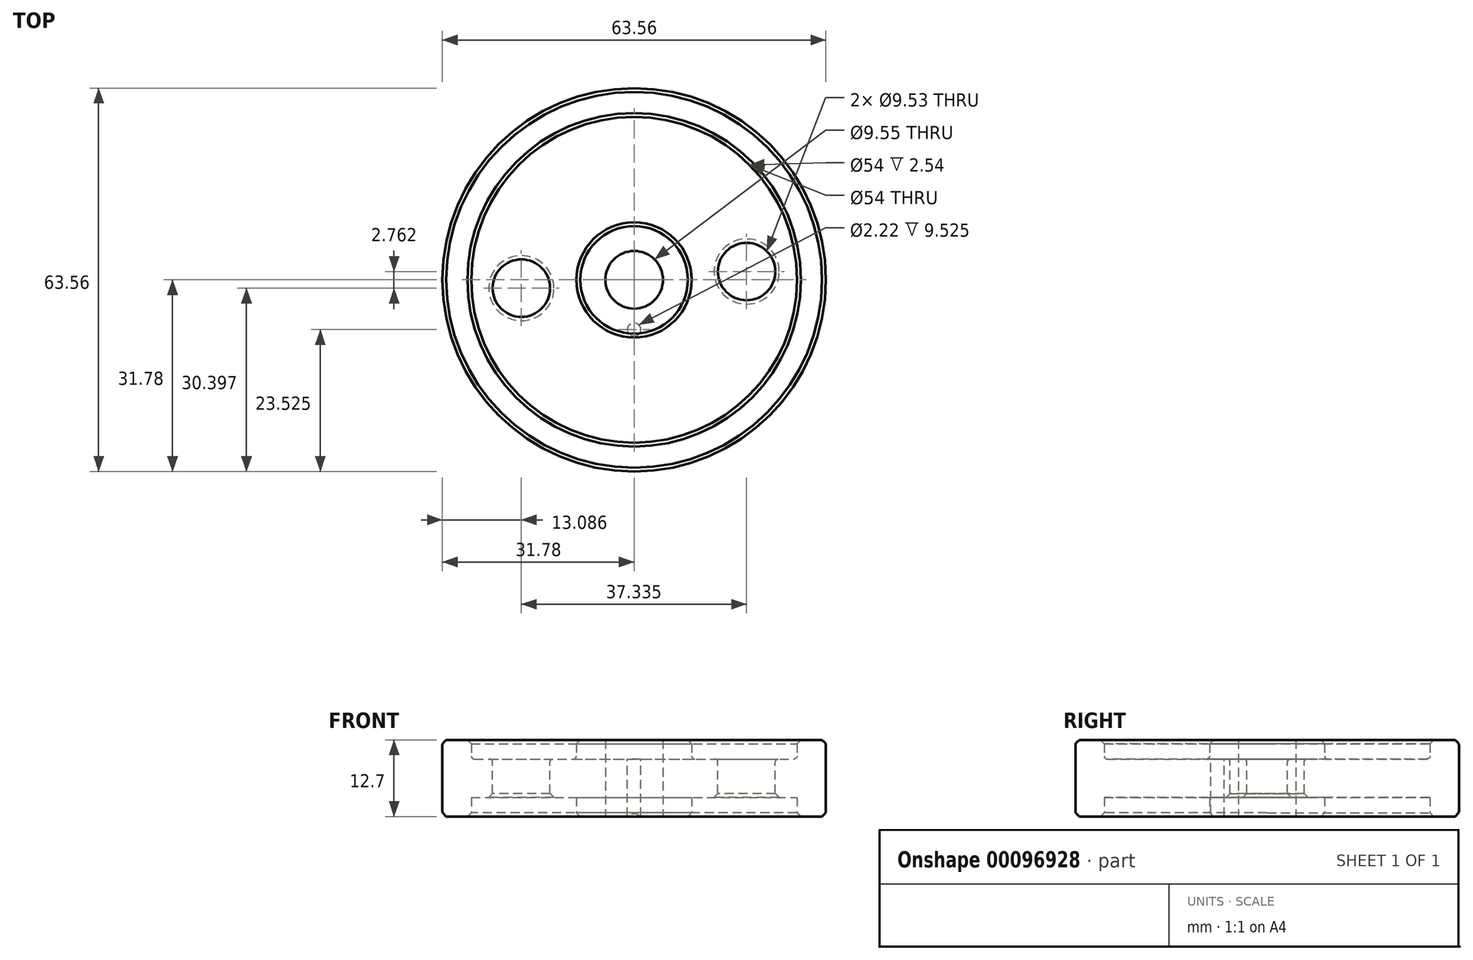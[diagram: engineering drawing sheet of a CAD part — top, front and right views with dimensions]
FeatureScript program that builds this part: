
annotation { "Feature Type Name" : "Feature", "Feature Type Description" : "" }
export const myFeature = defineFeature(function(context is Context, id is Id, definition is map)
    precondition{}
    {
        {
            var Q0;
            Q0=qCreatedBy(makeId("Front.planeOp"),FACE);
            var sketch = newSketch(context, id + "F0", { "sketchPlane" : qUnion([Q0])});
            skLineSegment(sketch, "E0", {"start": v(0, 0) * mm, "end": v(0, 8.6) * mm, "construction": true});
            skLineSegment(sketch, "E1", {"start": v(0, 0) * mm, "end": v(4.78, 0) * mm, "construction": true});
            skLineSegment(sketch, "E2", {"start": v(4.78, 0) * mm, "end": v(4.78, 12.7) * mm});
            skLineSegment(sketch, "E3", {"start": v(4.78, 12.7) * mm, "end": v(9.55, 12.7) * mm});
            skLineSegment(sketch, "E4", {"start": v(9.55, 12.7) * mm, "end": v(9.55, 9.53) * mm});
            skLineSegment(sketch, "E5", {"start": v(9.55, 9.53) * mm, "end": v(27, 9.53) * mm});
            skLineSegment(sketch, "E6", {"start": v(27, 9.53) * mm, "end": v(27, 12.7) * mm});
            skLineSegment(sketch, "E7", {"start": v(27, 12.7) * mm, "end": v(31.78, 12.7) * mm});
            skLineSegment(sketch, "E8", {"start": v(31.78, 12.7) * mm, "end": v(31.78, 0) * mm});
            skLineSegment(sketch, "E9", {"start": v(31.78, 0) * mm, "end": v(27, 0) * mm});
            skLineSegment(sketch, "E10", {"start": v(27, 0) * mm, "end": v(27, 3.18) * mm});
            skLineSegment(sketch, "E11", {"start": v(27, 3.18) * mm, "end": v(9.55, 3.18) * mm});
            skLineSegment(sketch, "E12", {"start": v(9.55, 3.18) * mm, "end": v(9.55, 0) * mm});
            skLineSegment(sketch, "E13", {"start": v(9.55, 0) * mm, "end": v(4.78, 0) * mm});
            skSolve(sketch);
        }
        {
            var Q0;
            Q0=makeQuery(id+"F0.imprint","IMPRINT",FACE,{"disambiguationData":[TD([[makeQuery(id+"F0.imprint","IMPRINT",EDGE,{"derivedFrom":sQuery(id+"F0.wireOp",EDGE,"E2")}),-1.0]])]});
            var Q1;
            Q1=sQuery(id+"F0.wireOp",EDGE,"E0");
            revolve(context, id + "F1", {"entities" : qUnion([Q0]), "axis" : qUnion([Q1]), "revolveType" : RevolveType.FULL});
        }
        {
            var Q0;
            Q0=makeQuery(id+"F1.opRevolve","SWEPT_FACE",FACE,{"disambiguationData":[OSD([sQuery(id+"F0.wireOp",EDGE,"E5")])]});
            var sketch = newSketch(context, id + "F2", { "sketchPlane" : qUnion([Q0])});
            skLineSegment(sketch, "E14", {"start": v(0, 0) * mm, "end": v(-47.23, -3.5) * mm, "construction": true});
            skLineSegment(sketch, "E15", {"start": v(0, 0) * mm, "end": v(41.04, 3.04) * mm, "construction": true});
            skCircle(sketch, "E16", {"center": v(-18.7, -1.38) * mm, "radius": 4.76 * mm});
            skCircle(sketch, "E17", {"center": v(18.64, 1.38) * mm, "radius": 4.76 * mm});
            skSolve(sketch);
        }
        {
            var Q0;
            Q0 = qSketchRegion(id + "F2", true);
            extrude(context, id + "F3", {"entities" : qUnion([Q0]), "operationType" : NewBodyOperationType.REMOVE, "endBound" : BoundingType.THROUGH_ALL, "oppositeDirection" : true, "depth" : 25.4 * mm});
        }
        {
            var Q0;
            Q0=makeQuery(id+"F3.boolean.opBoolean","COPY",EDGE,{"derivedFrom":makeQuery(id+"F3.opExtrude","CAP_EDGE",EDGE,{"disambiguationData":[OSD([sQuery(id+"F2.wireOp",EDGE,"E16")])],"isStart":true})});
            var Q1;
            Q1=makeQuery(id+"F3.boolean.opBoolean","COPY",EDGE,{"derivedFrom":makeQuery(id+"F3.opExtrude","CAP_EDGE",EDGE,{"disambiguationData":[OSD([sQuery(id+"F2.wireOp",EDGE,"E17")])],"isStart":true})});
            var Q2;
            Q2=makeQuery(id+"F1.opRevolve","SWEPT_EDGE",EDGE,{"disambiguationData":[OSD([sQuery(id+"F0.wireOp",EDGE,"E3"),sQuery(id+"F0.wireOp",EDGE,"E4")])]});
            chamfer(context, id + "F4", {"entities" : qUnion([Q0, Q1, Q2]), "width" : 0.64 * mm, "tangentPropagation" : true});
        }
        {
            var Q0;
            Q0=makeQuery(id+"F1.opRevolve","SWEPT_EDGE",EDGE,{"disambiguationData":[OSD([sQuery(id+"F0.wireOp",EDGE,"E6"),sQuery(id+"F0.wireOp",EDGE,"E7")])]});
            var Q1;
            Q1=makeQuery(id+"F1.opRevolve","SWEPT_EDGE",EDGE,{"disambiguationData":[OSD([sQuery(id+"F0.wireOp",EDGE,"E7"),sQuery(id+"F0.wireOp",EDGE,"E8")])]});
            chamfer(context, id + "F5", {"entities" : qUnion([Q0, Q1]), "width" : 0.64 * mm, "tangentPropagation" : true});
        }
        {
            var Q0;
            Q0=makeQuery(id+"F1.opRevolve","SWEPT_EDGE",EDGE,{"disambiguationData":[OSD([sQuery(id+"F0.wireOp",EDGE,"E8"),sQuery(id+"F0.wireOp",EDGE,"E9")])]});
            var Q1;
            Q1=makeQuery(id+"F1.opRevolve","SWEPT_EDGE",EDGE,{"disambiguationData":[OSD([sQuery(id+"F0.wireOp",EDGE,"E9"),sQuery(id+"F0.wireOp",EDGE,"E10")])]});
            var Q2;
            Q2=makeQuery(id+"F3.boolean.opBoolean","INTERSECT",EDGE,{"derivedFrom":[makeQuery(id+"F1.opRevolve","SWEPT_FACE",FACE,{"disambiguationData":[OSD([sQuery(id+"F0.wireOp",EDGE,"E11")])]}),makeQuery(id+"F3.opExtrude","SWEPT_FACE",FACE,{"disambiguationData":[OSD([sQuery(id+"F2.wireOp",EDGE,"E17")])]})]});
            var Q3;
            Q3=makeQuery(id+"F1.opRevolve","SWEPT_EDGE",EDGE,{"disambiguationData":[OSD([sQuery(id+"F0.wireOp",EDGE,"E12"),sQuery(id+"F0.wireOp",EDGE,"E13")])]});
            var Q4;
            Q4=makeQuery(id+"F3.boolean.opBoolean","INTERSECT",EDGE,{"derivedFrom":[makeQuery(id+"F1.opRevolve","SWEPT_FACE",FACE,{"disambiguationData":[OSD([sQuery(id+"F0.wireOp",EDGE,"E11")])]}),makeQuery(id+"F3.opExtrude","SWEPT_FACE",FACE,{"disambiguationData":[OSD([sQuery(id+"F2.wireOp",EDGE,"E16")])]})]});
            chamfer(context, id + "F6", {"entities" : qUnion([Q0, Q1, Q2, Q3, Q4]), "width" : 0.64 * mm, "tangentPropagation" : true});
        }
        {
            var Q0;
            Q0=makeQuery(id+"F1.opRevolve","SWEPT_FACE",FACE,{"disambiguationData":[OSD([sQuery(id+"F0.wireOp",EDGE,"E5")])]});
            var sketch = newSketch(context, id + "F7", { "sketchPlane" : qUnion([Q0])});
            skCircle(sketch, "E18", {"center": v(0, -8.26) * mm, "radius": 1.11 * mm});
            skSolve(sketch);
        }
        {
            var Q0;
            Q0 = qSketchRegion(id + "F7", true);
            extrude(context, id + "F8", {"entities" : qUnion([Q0]), "operationType" : NewBodyOperationType.REMOVE, "oppositeDirection" : true, "depth" : 9.65 * mm});
        }
        {
            var Q0;
            Q0=makeQuery(id+"F1.opRevolve","SWEPT_FACE",FACE,{"disambiguationData":[OSD([sQuery(id+"F0.wireOp",EDGE,"E5")])]});
            var sketch = newSketch(context, id + "F9", { "sketchPlane" : qUnion([Q0])});
            skCircle(sketch, "E19", {"center": v(0, -8.24) * mm, "radius": 1.09 * mm});
            skSolve(sketch);
        }
        {
            var Q0;
            Q0 = qSketchRegion(id + "F9", true);
            extrude(context, id + "F10", {"entities" : qUnion([Q0]), "operationType" : NewBodyOperationType.REMOVE, "oppositeDirection" : true, "depth" : 9.52 * mm});
        }
        {
            var Q0;
            Q0=makeQuery(id+"F1.opRevolve","SWEPT_FACE",FACE,{"disambiguationData":[OSD([sQuery(id+"F0.wireOp",EDGE,"E5")])]});
            var Q1;
            Q1=makeQuery(id+"F1.opRevolve","SWEPT_FACE",FACE,{"disambiguationData":[OSD([sQuery(id+"F0.wireOp",EDGE,"E8")])]});
            var Q2;
            Q2=makeQuery(id+"F1.opRevolve","SWEPT_EDGE",EDGE,{"disambiguationData":[OSD([sQuery(id+"F0.wireOp",EDGE,"E5"),sQuery(id+"F0.wireOp",EDGE,"E6")])]});
            var Q3;
            Q3=makeQuery(id+"F1.opRevolve","SWEPT_EDGE",EDGE,{"disambiguationData":[OSD([sQuery(id+"F0.wireOp",EDGE,"E4"),sQuery(id+"F0.wireOp",EDGE,"E5")])]});
            fillet(context, id + "F11", {"entities" : qUnion([Q0, Q1, Q2, Q3]), "radius" : 0.5 * mm, "tangentPropagation" : true, "allowEdgeOverflow" : false});
        }
    });
